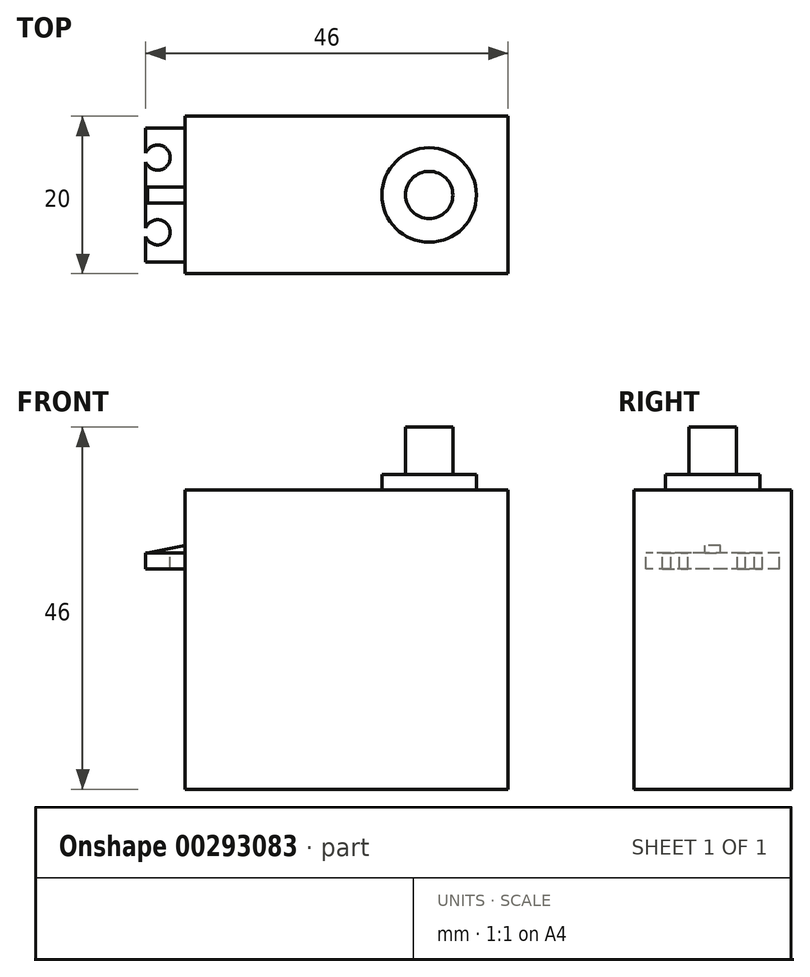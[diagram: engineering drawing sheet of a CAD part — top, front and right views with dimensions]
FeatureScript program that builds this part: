
annotation { "Feature Type Name" : "Feature", "Feature Type Description" : "" }
export const myFeature = defineFeature(function(context is Context, id is Id, definition is map)
    precondition{}
    {
        {
            var Q0;
            Q0=qCreatedBy(makeId("Top.planeOp"),FACE);
            var sketch = newSketch(context, id + "F0", { "sketchPlane" : qUnion([Q0])});
            skLineSegment(sketch, "E0.bottom", {"start": v(-20.5, 10) * mm, "end": v(20.5, 10) * mm});
            skLineSegment(sketch, "E0.top", {"start": v(-20.5, -10) * mm, "end": v(20.5, -10) * mm});
            skLineSegment(sketch, "E0.left", {"start": v(-20.5, 10) * mm, "end": v(-20.5, -10) * mm});
            skLineSegment(sketch, "E0.right", {"start": v(20.5, 10) * mm, "end": v(20.5, -10) * mm});
            skLineSegment(sketch, "E1", {"start": v(-67.55, 0) * mm, "end": v(64.9, 0) * mm, "construction": true});
            skLineSegment(sketch, "E2", {"start": v(0, 36.7) * mm, "end": v(0, -39.8) * mm, "construction": true});
            skPoint(sketch, "E3", {"position": v(0, 10) * mm});
            skPoint(sketch, "E4", {"position": v(-20.5, 0) * mm});
            skCircle(sketch, "E5", {"center": v(10.5, 0) * mm, "radius": 6 * mm});
            skCircle(sketch, "E6", {"center": v(10.5, 0) * mm, "radius": 3 * mm});
            skLineSegment(sketch, "E7.bottom", {"start": v(-20.5, 8.5) * mm, "end": v(-25.5, 8.5) * mm});
            skLineSegment(sketch, "E7.top", {"start": v(-20.5, -8.5) * mm, "end": v(-25.5, -8.5) * mm});
            skLineSegment(sketch, "E7.left", {"start": v(-20.5, 8.5) * mm, "end": v(-20.5, -8.5) * mm});
            skLineSegment(sketch, "E7.right", {"start": v(-25.5, 8.5) * mm, "end": v(-25.5, -8.5) * mm});
            skLineSegment(sketch, "E8", {"start": v(-25.5, 4.75) * mm, "end": v(-20.5, 4.75) * mm, "construction": true});
            skCircle(sketch, "E9", {"center": v(-24, 4.75) * mm, "radius": 1.6 * mm});
            skLineSegment(sketch, "E10", {"start": v(-25.5, -4.75) * mm, "end": v(-20.5, -4.75) * mm, "construction": true});
            skCircle(sketch, "E11", {"center": v(-24, -4.75) * mm, "radius": 1.6 * mm});
            skLineSegment(sketch, "E12", {"start": v(-24, 4.75) * mm, "end": v(-24, -4.75) * mm, "construction": true});
            skLineSegment(sketch, "E13", {"start": v(-25.25, 1) * mm, "end": v(-20.5, 1) * mm});
            skLineSegment(sketch, "E14", {"start": v(-25.25, -1) * mm, "end": v(-20.5, -1) * mm});
            skLineSegment(sketch, "E15", {"start": v(-25.25, 1) * mm, "end": v(-25.25, -1) * mm});
            skSolve(sketch);
        }
        {
            var Q0;
            Q0=makeQuery(id+"F0.imprint","IMPRINT",FACE,{"disambiguationData":[TD([[makeQuery(id+"F0.imprint","IMPRINT",EDGE,{"derivedFrom":sQuery(id+"F0.wireOp",EDGE,"E0.bottom")}),-1.0]])]});
            var Q1;
            Q1=makeQuery(id+"F0.imprint","IMPRINT",FACE,{"disambiguationData":[TD([[makeQuery(id+"F0.imprint","IMPRINT",EDGE,{"derivedFrom":sQuery(id+"F0.wireOp",EDGE,"E5")}),1.0]])]});
            var Q2;
            Q2=makeQuery(id+"F0.imprint","IMPRINT",FACE,{"disambiguationData":[TD([[makeQuery(id+"F0.imprint","IMPRINT",EDGE,{"derivedFrom":sQuery(id+"F0.wireOp",EDGE,"E6")}),1.0]])]});
            extrude(context, id + "F1", {"entities" : qUnion([Q0, Q1, Q2]), "oppositeDirection" : true, "depth" : 38 * mm});
        }
        {
            var Q0;
            Q0=makeQuery(id+"F0.imprint","IMPRINT",FACE,{"disambiguationData":[TD([[makeQuery(id+"F0.imprint","IMPRINT",EDGE,{"derivedFrom":sQuery(id+"F0.wireOp",EDGE,"E5")}),1.0]])]});
            extrude(context, id + "F2", {"entities" : qUnion([Q0]), "operationType" : NewBodyOperationType.ADD, "depth" : 2 * mm});
        }
        {
            var Q0;
            Q0=makeQuery(id+"F0.imprint","IMPRINT",FACE,{"disambiguationData":[TD([[makeQuery(id+"F0.imprint","IMPRINT",EDGE,{"derivedFrom":sQuery(id+"F0.wireOp",EDGE,"E6")}),1.0]])]});
            extrude(context, id + "F3", {"entities" : qUnion([Q0]), "operationType" : NewBodyOperationType.ADD, "depth" : 8 * mm});
        }
        {
            var Q0;
            {var subQ5=sQuery(id+"F0.wireOp",EDGE,"E7.bottom");Q0=makeQuery(id+"F0.imprint","IMPRINT",FACE,{"disambiguationData":[TD([[makeQuery(id+"F0.imprint","IMPRINT",EDGE,{"derivedFrom":subQ5}),1.0]])]});}
            var Q1;
            {var subQ0=sQuery(id+"F0.wireOp",EDGE,"E13");Q1=makeQuery(id+"F0.imprint","IMPRINT",FACE,{"disambiguationData":[TD([[makeQuery(id+"F0.imprint","IMPRINT",EDGE,{"derivedFrom":subQ0}),-1.0]])]});}
            var Q2;
            {var subQ5=sQuery(id+"F0.wireOp",EDGE,"E7.top");Q2=makeQuery(id+"F0.imprint","IMPRINT",FACE,{"disambiguationData":[TD([[makeQuery(id+"F0.imprint","IMPRINT",EDGE,{"derivedFrom":subQ5}),-1.0]])]});}
            extrude(context, id + "F4", {"entities" : qUnion([Q0, Q1, Q2]), "operationType" : NewBodyOperationType.ADD, "oppositeDirection" : true, "depth" : 10 * mm, "hasSecondDirection" : true, "secondDirectionOppositeDirection" : true, "secondDirectionDepth" : 8 * mm});
        }
        {
            var Q0;
            {var subQ0=sQuery(id+"F0.wireOp",EDGE,"E13");Q0=makeQuery(id+"F0.imprint","IMPRINT",FACE,{"disambiguationData":[TD([[makeQuery(id+"F0.imprint","IMPRINT",EDGE,{"derivedFrom":subQ0}),-1.0]])]});}
            var Q1;
            Q1=makeQuery(id+"F4.opExtrude","CAP_FACE",FACE,{"disambiguationData":[OSD([sQuery(id+"F0.wireOp",EDGE,"E7.bottom"),sQuery(id+"F0.wireOp",EDGE,"E7.top"),sQuery(id+"F0.wireOp",EDGE,"E7.left"),sQuery(id+"F0.wireOp",EDGE,"E7.right"),sQuery(id+"F0.wireOp",EDGE,"E9"),sQuery(id+"F0.wireOp",EDGE,"E11")])],"isStart":true});
            extrude(context, id + "F5", {"entities" : qUnion([Q0]), "operationType" : NewBodyOperationType.ADD, "endBound" : BoundingType.UP_TO_SURFACE, "oppositeDirection" : true, "endBoundEntityFace" : qUnion([Q1]), "depth" : 5 * mm, "hasSecondDirection" : true, "secondDirectionOppositeDirection" : true, "secondDirectionDepth" : 7 * mm});
        }
        {
            var Q0;
            Q0=makeQuery(id+"F5.opExtrude","CAP_EDGE",EDGE,{"disambiguationData":[OSD([sQuery(id+"F0.wireOp",EDGE,"E15")])],"isStart":true});
            chamfer(context, id + "F6", {"entities" : qUnion([Q0]), "chamferType" : ChamferType.TWO_OFFSETS, "width1" : 4.75 * mm, "oppositeDirection" : false, "width2" : 1 * mm, "tangentPropagation" : true});
        }
    });
